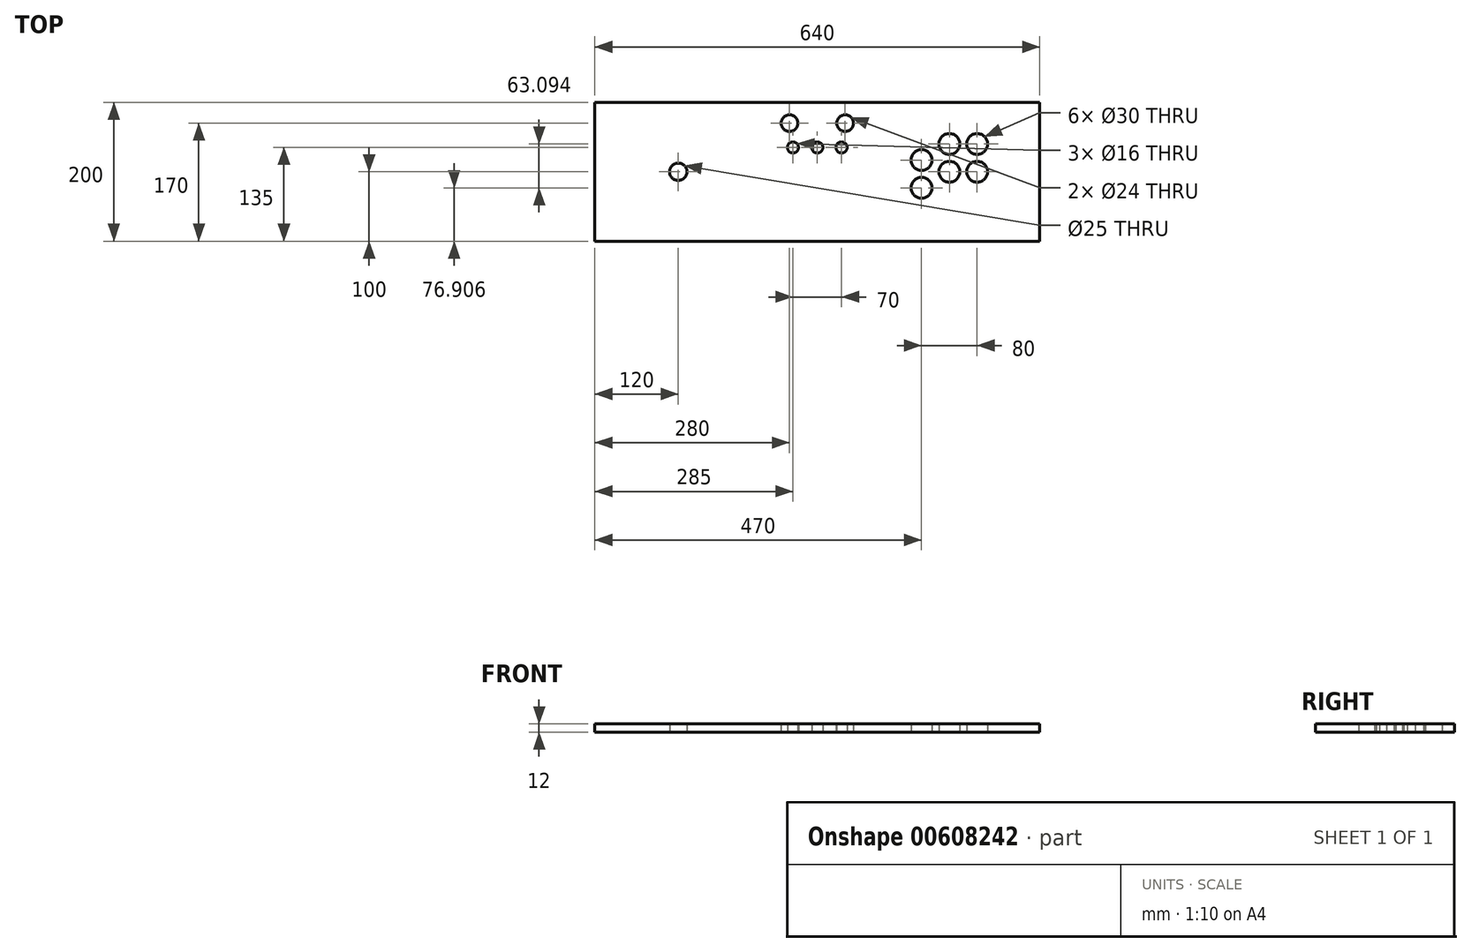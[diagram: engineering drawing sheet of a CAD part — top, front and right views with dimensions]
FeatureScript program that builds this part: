
annotation { "Feature Type Name" : "Feature", "Feature Type Description" : "" }
export const myFeature = defineFeature(function(context is Context, id is Id, definition is map)
    precondition{}
    {
        {
            var Q0;
            Q0=qCreatedBy(makeId("Top.planeOp"),FACE);
            var sketch = newSketch(context, id + "F0", { "sketchPlane" : qUnion([Q0])});
            skLineSegment(sketch, "E0.bottom", {"start": v(-320, 100) * mm, "end": v(320, 100) * mm});
            skLineSegment(sketch, "E0.top", {"start": v(-320, -100) * mm, "end": v(320, -100) * mm});
            skLineSegment(sketch, "E0.left", {"start": v(-320, 100) * mm, "end": v(-320, -100) * mm});
            skLineSegment(sketch, "E0.right", {"start": v(320, 100) * mm, "end": v(320, -100) * mm});
            skPoint(sketch, "E0.middle", {"position": v(0, 0) * mm});
            skCircle(sketch, "E1", {"center": v(-200, 0) * mm, "radius": 12.5 * mm});
            skCircle(sketch, "E2", {"center": v(150, 16.9) * mm, "radius": 15 * mm});
            skCircle(sketch, "E3", {"center": v(150, -23.1) * mm, "radius": 15 * mm});
            skCircle(sketch, "E4", {"center": v(190, 40) * mm, "radius": 15 * mm});
            skCircle(sketch, "E5", {"center": v(190, 0) * mm, "radius": 15 * mm});
            skCircle(sketch, "E6", {"center": v(230, 40) * mm, "radius": 15 * mm});
            skCircle(sketch, "E7", {"center": v(230, 0) * mm, "radius": 15 * mm});
            skLineSegment(sketch, "E8", {"start": v(150, 16.9) * mm, "end": v(233.37, 16.9) * mm, "construction": true});
            skLineSegment(sketch, "E9", {"start": v(150, 16.9) * mm, "end": v(190, 40) * mm, "construction": true});
            skLineSegment(sketch, "E10", {"start": v(150, -23.1) * mm, "end": v(181.54, -23.1) * mm, "construction": true});
            skLineSegment(sketch, "E11", {"start": v(150, -23.1) * mm, "end": v(190, 0) * mm, "construction": true});
            skLineSegment(sketch, "E12", {"start": v(190, 0) * mm, "end": v(150, 0) * mm, "construction": true});
            skLineSegment(sketch, "E13", {"start": v(0, 0) * mm, "end": v(-293.87, 0) * mm, "construction": true});
            skCircle(sketch, "E14", {"center": v(-40, 70) * mm, "radius": 12 * mm});
            skCircle(sketch, "E15.MirrorC", {"center": v(40, 70) * mm, "radius": 12 * mm});
            skCircle(sketch, "E16", {"center": v(0, 35) * mm, "radius": 8 * mm});
            skCircle(sketch, "E17", {"center": v(-35, 35) * mm, "radius": 8 * mm});
            skCircle(sketch, "E18", {"center": v(35, 35) * mm, "radius": 8 * mm});
            skSolve(sketch);
        }
        {
            var Q0;
            Q0 = qSketchRegion(id + "F0", true);
            extrude(context, id + "F1", {"entities" : qUnion([Q0]), "depth" : 12 * mm, "offsetDistance" : 25 * mm});
        }
    });
